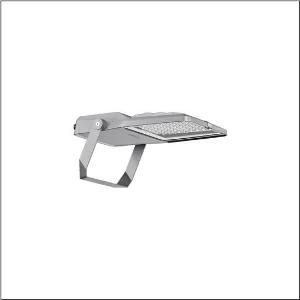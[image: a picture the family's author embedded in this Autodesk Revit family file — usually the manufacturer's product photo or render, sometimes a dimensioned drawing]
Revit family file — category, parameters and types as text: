
# Revit family: floodlight_fl_21_iq_mini___pl61_5xa7772c1c1a_a98f
name_source: partatom
category: Lighting Fixtures
units: mm (PartAtom-declared; Revit-internal decimal feet)

## family parameters
Cut with Voids When Loaded = No
Host = Face
Light Source = No
Part Type = Normal
Room Calculation Point = No
Round Connector Dimension = Use Diameter
Shared = No

## types (1)
- --- (1 x LED, 9930 lm, 87.2 W, 2200K)
    Apparent Load = 87 VA
    CIE Flux Codes = 33 65 98 100 100
    Color Rendering = 70
    Color Temperature = 2200K
    Default Elevation = 1800 mm
    Description = Floodlight FL 21 iQ mini, floodlight, primary light control with lens, of PMMA, primary optical cover: protective disc, of toughened safety glass, transparent, light distribution: PL61, light emission: direct distribution, installation type: surface-mounted, LED, High Power LED, rated luminous flux: 9.930lm, luminous efficacy: 114lm/W, light colour: 722, colour temperature: 2200K, control: Street-Remote, Auto-Match, Temp-Guard, Night-Set, Smart-Wire, Desk-Remote (wireless, voltage-free reading and setting of iQ features in the workshop via application-optimized NFC function/RFID function), optimised constant luminous flux control (CLO 2.0), with terminal, 6-pole, mains connection: 220..240V, AC, 50/60Hz, start of lifetime: 87W, end of service life: 92W, reduction: 40W, luminaire housing, of diecast aluminium, powder-coated, Siteco® metallic grey (DB 702S), corrosivity category C5 mid according to DIN EN ISO 12944, sealing non-destructively replaceable, mounting bracket, of steel, galvanised, powder-coated, Siteco® metallic grey (DB 702S), protection rating (complete): IP66, insulation class (complete): insulation class II (safety insulation), certification: CE, ENEC, VDE, protection symbol: D, impact resistance: IK08, permissible operating ambient temperature: -40..+40°C, permissible operating ambient temperature for outdoor applications: -40..+50°C, standard: DIN EN 12944, LABS conformity tested according to VDMA 24364:2018-05, packaging unit: 1 piece

Light Distribution: PL61
    Height = 70 mm
    Lamp = 1 x LED
    Lamp Light Flux = 9930 lm
    Lamp Power = 87.2 W
    Lamp count = 1
    Length = 485 mm
    Luminous efficacy = 114 lm/W
    Manufacturer = Siteco
    ModVariant = No
    Model = 5XA7772C1C1A
    Number of Poles = 1
    OnlyDefault = Yes
    Power Factor = 1
    Product Name = Floodlight FL 21 iQ mini | PL61
    Product group = floodlight | pylon annexe
    ProductGroupID = 6200
    Protection Class = Protection class II
    Protection Degree = IP 66
    RLX_Detail_Level = 1
    RLX_Emergency_Light_Flux = 0 lm
    RLX_Emergency_Type = 0
    RLX_Emergency_Type_DB = No
    RlxData = <blob elided: 96289 chars, md5=01e0caba>
    Socket = socket
    Standby Power = 0 W
    System Light Flux = 9930 lm
    System Power = 87 W
    Type Comments = factory setting: luminous flux: 100 % | dim-lin: 254 | 456 mA
    Type Image = l_1006845.jpg
    URL = http://relux.com
    VarID = @adj_106227
    Voltage = 0 V
    Weight = 0.00 kg
    Width = 337 mm

## geometry (parser evidence)
native form markers: Blend x4, Sweep x12
no freeform markers — native parametric forms only
